# Revit family: NLRS_90_SI_Fietsenrek-FalcoSound_Dubbelzijdig_flc_FLC
name_source: partatom
category: Specialty Equipment
units: mm (PartAtom-declared; Revit-internal decimal feet)

## family parameters
Always vertical = Yes
Cut with Voids When Loaded = No
Enable Cutting in Views = Yes
Maintain Annotation Orientation = No
Part Type = Normal
Room Calculation Point = No
Round Connector Dimension = Use Diameter
Shared = No
Work Plane-Based = No

## types (10) — shared parameters
Achterkant fiets = 1557 mm  [stored 5.10827 ft]
Looppad = 3057 mm  [stored 10.0295 ft]
Manufacturer = Falco BV
Muur = 374 mm  [stored 1.22703 ft]
NLRS_C_diepte = 400 mm  [stored 1.31234 ft]
NLRS_C_leverancier = Falco B.V.
NLRS_C_leverancier_url = www.falco.nl

## per-type parameters (varying)
| type | NLRS_C_lengte | aantal_plaatsen | hartafstand | hoh_dubbel | hoh_half |
| Sound dubbelzijdig hoh 375 4 plaatsen l=750 | 750 mm  [stored 2.46063 ft] | 4 | 375 mm  [stored 1.23031 ft] | 750 mm  [stored 2.46063 ft] | 188 mm  [stored 0.616798 ft] |
| Sound dubbelzijdig hoh 375 6 plaatsen l=1125 | 1125 mm | 6 | 375 mm  [stored 1.23031 ft] | 750 mm  [stored 2.46063 ft] | 188 mm  [stored 0.616798 ft] |
| Sound dubbelzijdig hoh 375 8 plaatsen l=1500 | 1500 mm  [stored 4.92126 ft] | 8 | 375 mm  [stored 1.23031 ft] | 750 mm  [stored 2.46063 ft] | 188 mm  [stored 0.616798 ft] |
| Sound dubbelzijdig hoh 375 10 plaatsen l=1875 | 1875 mm  [stored 6.15157 ft] | 10 | 375 mm  [stored 1.23031 ft] | 750 mm  [stored 2.46063 ft] | 188 mm  [stored 0.616798 ft] |
| Sound dubbelzijdig hoh 375 12 plaatsen l=2250 | 2250 mm | 12 | 375 mm  [stored 1.23031 ft] | 750 mm  [stored 2.46063 ft] | 188 mm  [stored 0.616798 ft] |
| Sound dubbelzijdig hoh 400 4 plaatsen l=800 | 800 mm  [stored 2.62467 ft] | 4 | 400 mm  [stored 1.31234 ft] | 800 mm  [stored 2.62467 ft] | 200 mm  [stored 0.656168 ft] |
| Sound dubbelzijdig hoh 400 6 plaatsen l=1200 | 1200 mm | 6 | 400 mm  [stored 1.31234 ft] | 800 mm  [stored 2.62467 ft] | 200 mm  [stored 0.656168 ft] |
| Sound dubbelzijdig hoh 400 8 plaatsen l=1600 | 1600 mm  [stored 5.24934 ft] | 8 | 400 mm  [stored 1.31234 ft] | 800 mm  [stored 2.62467 ft] | 200 mm  [stored 0.656168 ft] |
| Sound dubbelzijdig hoh 400 10 plaatsen l=2000 | 2000 mm  [stored 6.56168 ft] | 10 | 400 mm  [stored 1.31234 ft] | 800 mm  [stored 2.62467 ft] | 200 mm  [stored 0.656168 ft] |
| Sound dubbelzijdig hoh 400 12 plaatsen l=2400 | 2400 mm | 12 | 400 mm  [stored 1.31234 ft] | 800 mm  [stored 2.62467 ft] | 200 mm  [stored 0.656168 ft] |

note: [stored X ft] marks values corroborated as IEEE doubles in the binary element streams (Revit-internal decimal feet)

## geometry (parser evidence)
native form markers: Sweep x8
no freeform markers — native parametric forms only
